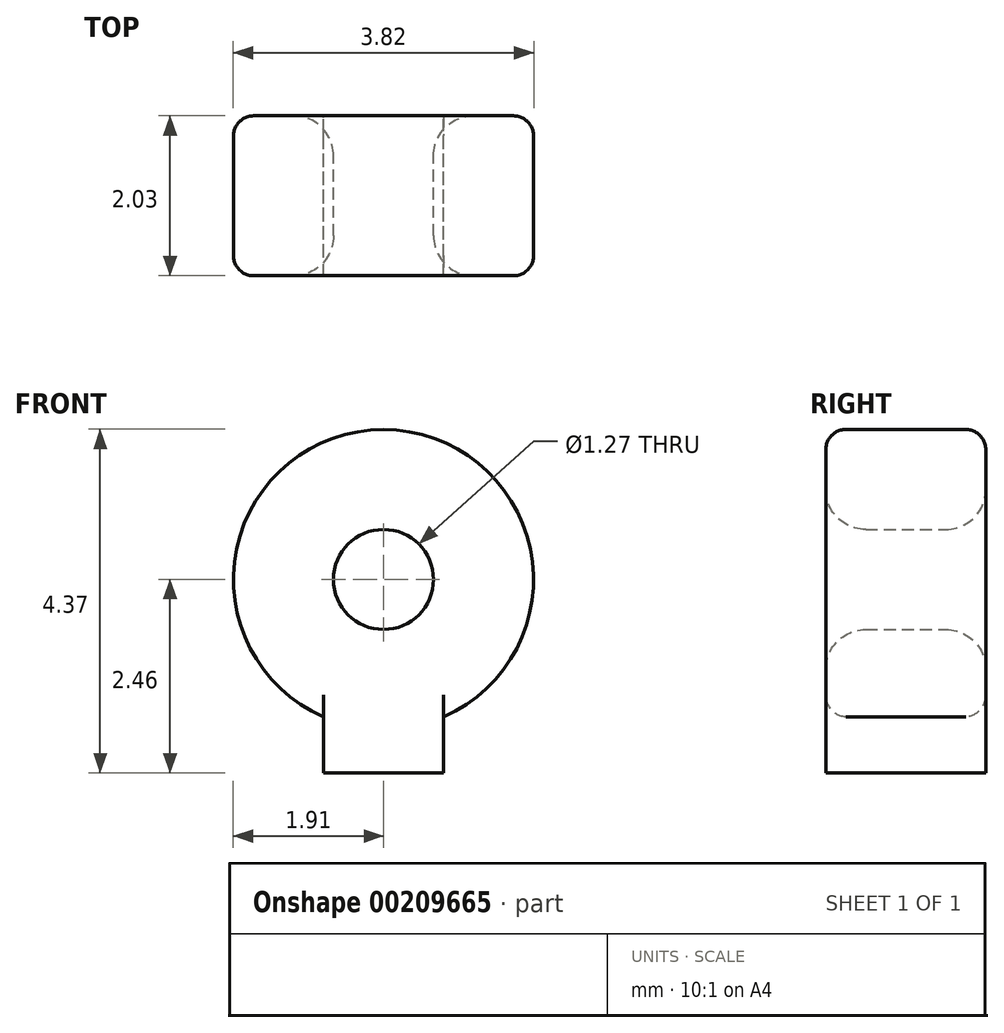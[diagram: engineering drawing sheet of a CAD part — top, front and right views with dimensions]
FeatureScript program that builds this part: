
annotation { "Feature Type Name" : "Feature", "Feature Type Description" : "" }
export const myFeature = defineFeature(function(context is Context, id is Id, definition is map)
    precondition{}
    {
        {
            var Q0;
            Q0=qCreatedBy(makeId("Front.planeOp"),FACE);
            var sketch = newSketch(context, id + "F2", { "sketchPlane" : qUnion([Q0])});
            skArc(sketch, "E0", {"start": v(0.76, -1.75) * mm, "mid": v(0, 1.9) * mm, "end": v(-0.76, -1.75) * mm});
            skCircle(sketch, "E1", {"center": v(0, 0) * mm, "radius": 0.64 * mm});
            skLineSegment(sketch, "E2.0", {"start": v(-0.76, -1.75) * mm, "end": v(-0.76, -2.46) * mm});
            skLineSegment(sketch, "E3.0", {"start": v(0.76, -1.75) * mm, "end": v(0.76, -2.46) * mm});
            skLineSegment(sketch, "E4", {"start": v(-0.76, -2.46) * mm, "end": v(0.76, -2.46) * mm});
            skPoint(sketch, "E5.orphan", {"position": v(0.76, -3.17) * mm});
            skPoint(sketch, "E6.orphan", {"position": v(-0.76, -3.17) * mm});
            skSolve(sketch);
        }
        {
            var Q0;
            Q0=makeQuery(id+"F2.imprint","IMPRINT",FACE,{"disambiguationData":[TD([[makeQuery(id+"F2.imprint","IMPRINT",EDGE,{"derivedFrom":sQuery(id+"F2.wireOp",EDGE,"E0")}),1.0]])]});
            extrude(context, id + "F0", {"entities" : qUnion([Q0]), "depth" : 2.03 * mm});
        }
        {
            var Q0;
            Q0=makeQuery(id+"F0.opExtrude","CAP_EDGE",EDGE,{"disambiguationData":[OSD([sQuery(id+"F2.wireOp",EDGE,"E1")])],"isStart":true});
            var Q1;
            Q1=makeQuery(id+"F0.opExtrude","CAP_EDGE",EDGE,{"disambiguationData":[OSD([sQuery(id+"F2.wireOp",EDGE,"E1")])],"isStart":false});
            fillet(context, id + "F3", {"entities" : qUnion([Q0, Q1]), "radius" : 0.5 * mm, "tangentPropagation" : true, "allowEdgeOverflow" : false});
        }
        {
            var Q0;
            Q0=makeQuery(id+"F0.opExtrude","CAP_EDGE",EDGE,{"disambiguationData":[OSD([sQuery(id+"F2.wireOp",EDGE,"E0")])],"isStart":false});
            var Q1;
            Q1=makeQuery(id+"F0.opExtrude","CAP_EDGE",EDGE,{"disambiguationData":[OSD([sQuery(id+"F2.wireOp",EDGE,"E0")])],"isStart":true});
            fillet(context, id + "F1", {"entities" : qUnion([Q0, Q1]), "radius" : 0.25 * mm, "tangentPropagation" : true, "allowEdgeOverflow" : false});
        }
    });
